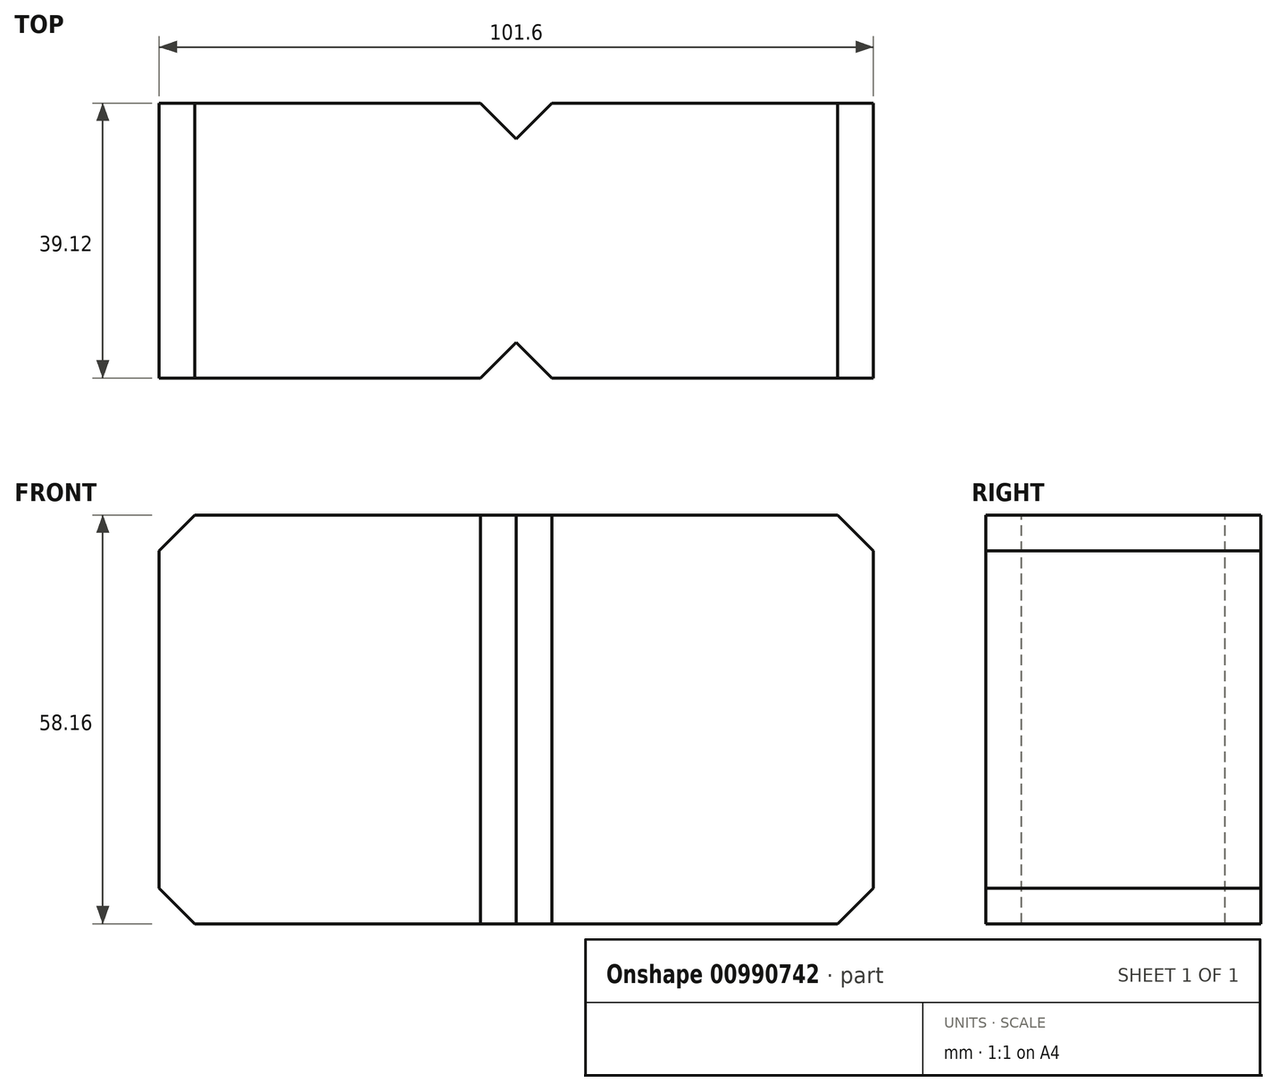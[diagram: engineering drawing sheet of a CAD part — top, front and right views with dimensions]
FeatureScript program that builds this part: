
annotation { "Feature Type Name" : "Feature", "Feature Type Description" : "" }
export const myFeature = defineFeature(function(context is Context, id is Id, definition is map)
    precondition{}
    {
        {
            var Q0;
            Q0=qCreatedBy(makeId("Front.planeOp"),FACE);
            var sketch = newSketch(context, id + "F0", { "sketchPlane" : qUnion([Q0])});
            skLineSegment(sketch, "E0.bottom", {"start": v(-25.4, 29.08) * mm, "end": v(25.4, 29.08) * mm});
            skLineSegment(sketch, "E0.top", {"start": v(-25.4, -29.08) * mm, "end": v(25.4, -29.08) * mm});
            skLineSegment(sketch, "E0.left", {"start": v(-25.4, 29.08) * mm, "end": v(-25.4, -29.08) * mm});
            skLineSegment(sketch, "E0.right", {"start": v(25.4, 29.08) * mm, "end": v(25.4, -29.08) * mm});
            skPoint(sketch, "E0.middle", {"position": v(0, 0) * mm});
            skSolve(sketch);
        }
        {
            var Q0;
            Q0=makeQuery(id+"F0.imprint","IMPRINT",FACE,{"disambiguationData":[TD([[makeQuery(id+"F0.imprint","IMPRINT",EDGE,{"derivedFrom":sQuery(id+"F0.wireOp",EDGE,"E0.bottom")}),-1.0]])]});
            extrude(context, id + "F1", {"entities" : qUnion([Q0]), "depth" : 19.56 * mm, "offsetDistance" : 25.4 * mm});
        }
        {
            var Q0;
            Q0=makeQuery(id+"F1.opExtrude","SWEPT_EDGE",EDGE,{"disambiguationData":[OSD([sQuery(id+"F0.wireOp",EDGE,"E0.bottom"),sQuery(id+"F0.wireOp",EDGE,"E0.right")])]});
            chamfer(context, id + "F2", {"entities" : qUnion([Q0]), "width" : 5.08 * mm, "tangentPropagation" : true});
        }
        {
            var Q0;
            Q0=makeQuery(id+"F1.opExtrude","SWEPT_EDGE",EDGE,{"disambiguationData":[OSD([sQuery(id+"F0.wireOp",EDGE,"E0.top"),sQuery(id+"F0.wireOp",EDGE,"E0.right")])]});
            var Q1;
            Q1=makeQuery(id+"F1.opExtrude","CAP_EDGE",EDGE,{"disambiguationData":[OSD([sQuery(id+"F0.wireOp",EDGE,"E0.left")])],"isStart":false});
            chamfer(context, id + "F3", {"entities" : qUnion([Q0, Q1]), "width" : 5.08 * mm, "tangentPropagation" : true});
        }
        {
            var Q0;
            Q0=makeQuery(id+"F1.opExtrude","SWEPT_BODY",BODY,{"disambiguationData":[OSD([sQuery(id+"F0.wireOp",EDGE,"E0.bottom"),sQuery(id+"F0.wireOp",EDGE,"E0.top"),sQuery(id+"F0.wireOp",EDGE,"E0.left"),sQuery(id+"F0.wireOp",EDGE,"E0.right")])]});
            var Q1;
            Q1=makeQuery(id+"F1.opExtrude","SWEPT_FACE",FACE,{"disambiguationData":[OSD([sQuery(id+"F0.wireOp",EDGE,"E0.left")])]});
            mirror(context, id + "F4", {"operationType" : NewBodyOperationType.ADD, "entities" : qUnion([Q0]), "mirrorPlane" : qUnion([Q1])});
        }
        {
            var Q0;
            Q0=makeQuery(id+"F1.opExtrude","SWEPT_BODY",BODY,{"disambiguationData":[OSD([sQuery(id+"F0.wireOp",EDGE,"E0.bottom"),sQuery(id+"F0.wireOp",EDGE,"E0.top"),sQuery(id+"F0.wireOp",EDGE,"E0.left"),sQuery(id+"F0.wireOp",EDGE,"E0.right")])]});
            var Q1;
            {var subQ0=makeQuery(id+"F1.opExtrude","CAP_FACE",FACE,{"disambiguationData":[OSD([sQuery(id+"F0.wireOp",EDGE,"E0.bottom"),sQuery(id+"F0.wireOp",EDGE,"E0.top"),sQuery(id+"F0.wireOp",EDGE,"E0.left"),sQuery(id+"F0.wireOp",EDGE,"E0.right")])],"isStart":true});Q1=makeQuery(id+"F4.boolean.opBoolean","MERGE",FACE,{"derivedFrom":[subQ0,makeQuery(id+"F4.opPattern","COPY",FACE,{"derivedFrom":subQ0,"instanceName":"1"})]});}
            mirror(context, id + "F5", {"operationType" : NewBodyOperationType.ADD, "entities" : qUnion([Q0]), "mirrorPlane" : qUnion([Q1])});
        }
    });
